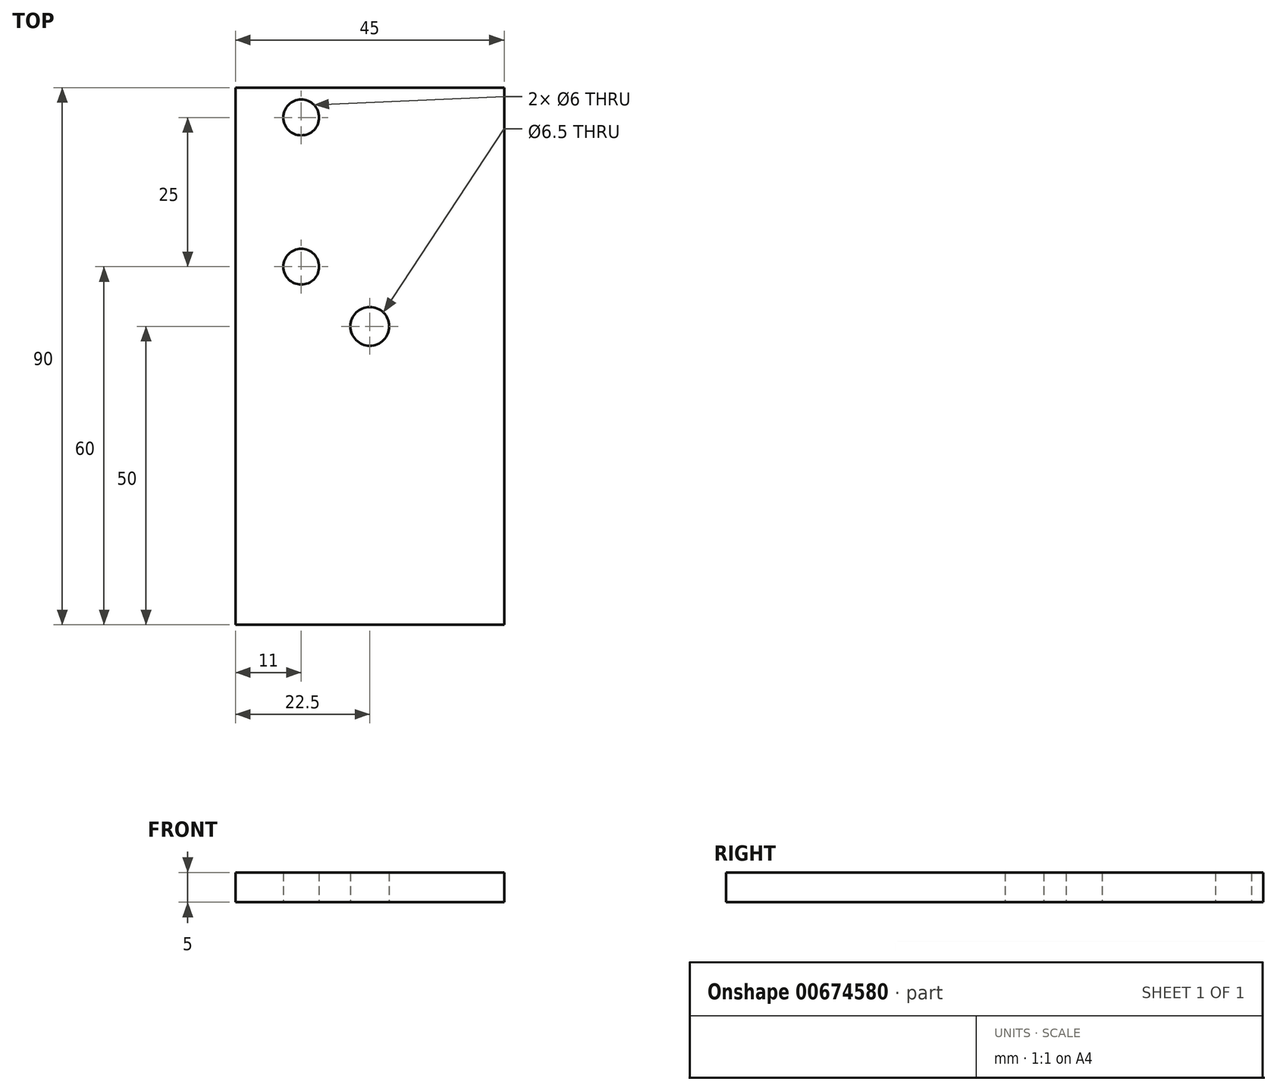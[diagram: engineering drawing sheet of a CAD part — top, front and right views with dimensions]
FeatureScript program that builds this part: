
annotation { "Feature Type Name" : "Feature", "Feature Type Description" : "" }
export const myFeature = defineFeature(function(context is Context, id is Id, definition is map)
    precondition{}
    {
        {
            var Q0;
            Q0=qCreatedBy(makeId("Top.planeOp"),FACE);
            var sketch = newSketch(context, id + "F0", { "sketchPlane" : qUnion([Q0])});
            skLineSegment(sketch, "E0.bottom", {"start": v(0, 0) * mm, "end": v(45, 0) * mm});
            skLineSegment(sketch, "E0.top", {"start": v(0, 90) * mm, "end": v(45, 90) * mm});
            skLineSegment(sketch, "E0.left", {"start": v(0, 0) * mm, "end": v(0, 90) * mm});
            skLineSegment(sketch, "E0.right", {"start": v(45, 0) * mm, "end": v(45, 90) * mm});
            skCircle(sketch, "E1", {"center": v(11, 85) * mm, "radius": 3 * mm});
            skCircle(sketch, "E2", {"center": v(11, 60) * mm, "radius": 3 * mm});
            skCircle(sketch, "E3", {"center": v(22.5, 50) * mm, "radius": 3.25 * mm});
            skPoint(sketch, "E4", {"position": v(22.5, 0) * mm});
            skSolve(sketch);
        }
        {
            var Q0;
            Q0=makeQuery(id+"F0.imprint","IMPRINT",FACE,{"disambiguationData":[TD([[makeQuery(id+"F0.imprint","IMPRINT",EDGE,{"derivedFrom":sQuery(id+"F0.wireOp",EDGE,"E0.bottom")}),1.0]])]});
            extrude(context, id + "F1", {"entities" : qUnion([Q0]), "depth" : 5 * mm, "offsetDistance" : 25 * mm});
        }
    });
